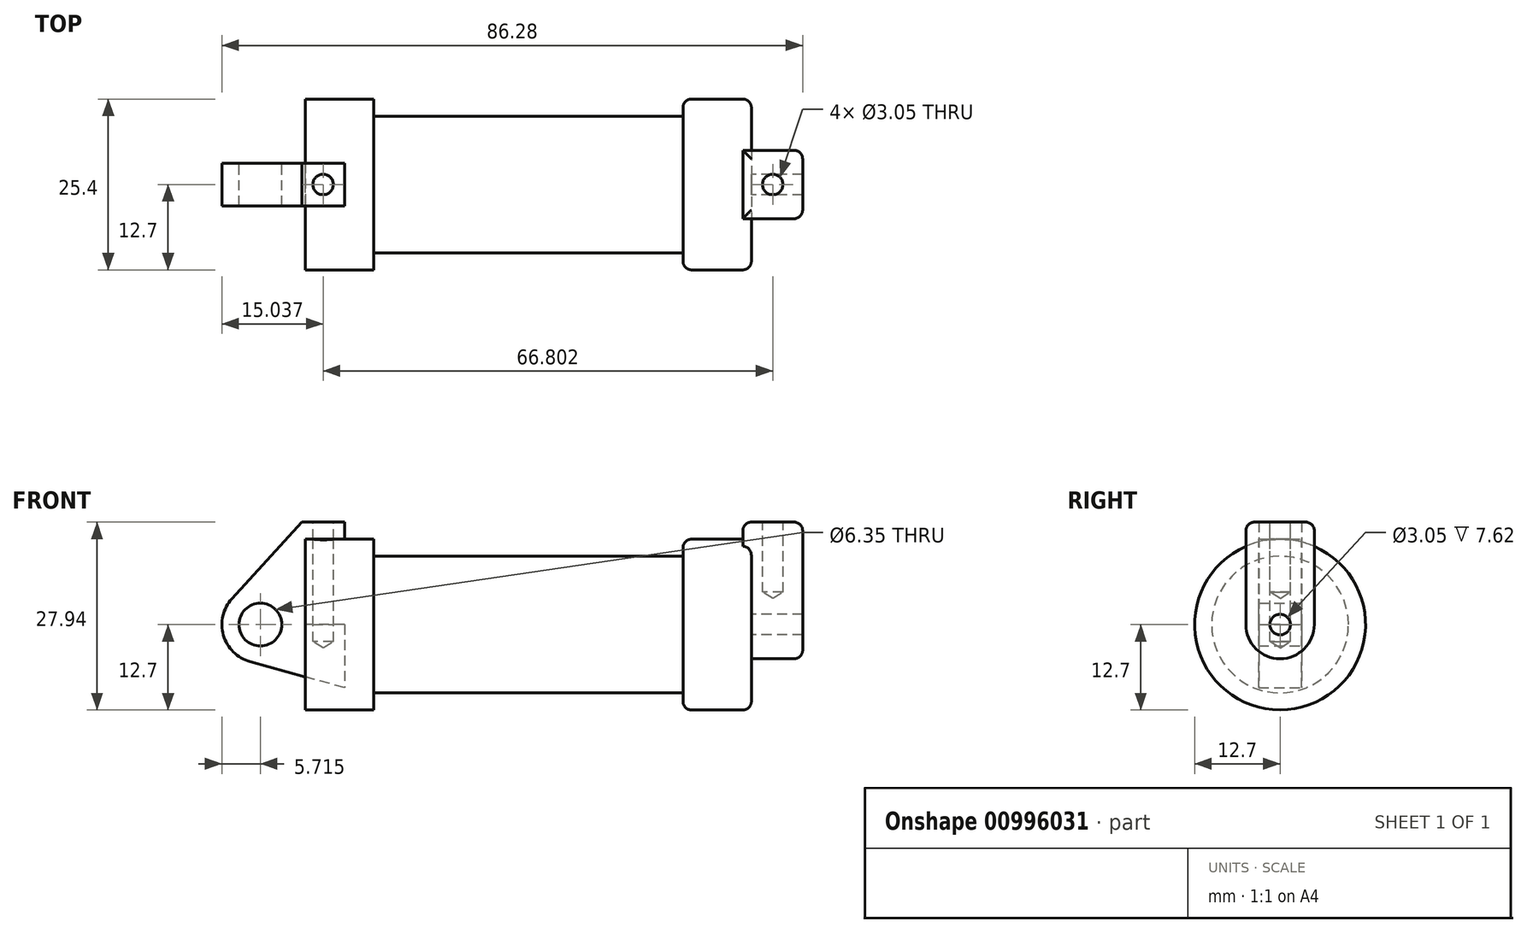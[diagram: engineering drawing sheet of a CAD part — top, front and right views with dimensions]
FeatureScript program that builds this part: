
annotation { "Feature Type Name" : "Feature", "Feature Type Description" : "" }
export const myFeature = defineFeature(function(context is Context, id is Id, definition is map)
    precondition{}
    {
        {
            var Q0;
            Q0=qCreatedBy(makeId("Front.planeOp"),FACE);
            var sketch = newSketch(context, id + "F0", { "sketchPlane" : qUnion([Q0])});
            skLineSegment(sketch, "E0", {"start": v(0, 0) * mm, "end": v(0, 12.7) * mm});
            skLineSegment(sketch, "E1", {"start": v(0, 12.7) * mm, "end": v(10.16, 12.7) * mm});
            skLineSegment(sketch, "E2", {"start": v(10.16, 12.7) * mm, "end": v(10.16, 10.16) * mm});
            skLineSegment(sketch, "E3", {"start": v(10.16, 10.16) * mm, "end": v(56.13, 10.16) * mm});
            skLineSegment(sketch, "E4", {"start": v(56.13, 10.16) * mm, "end": v(56.13, 12.7) * mm});
            skLineSegment(sketch, "E5", {"start": v(56.13, 12.7) * mm, "end": v(66.3, 12.7) * mm});
            skLineSegment(sketch, "E6", {"start": v(66.3, 12.7) * mm, "end": v(66.3, 0) * mm});
            skLineSegment(sketch, "E7", {"start": v(66.3, 0) * mm, "end": v(0, 0) * mm});
            skLineSegment(sketch, "E8", {"start": v(5.84, 15.24) * mm, "end": v(-0.5, 15.24) * mm});
            skLineSegment(sketch, "E9", {"start": v(-0.5, 15.24) * mm, "end": v(-10.88, 3.85) * mm});
            skLineSegment(sketch, "E10", {"start": v(0, 0) * mm, "end": v(-6.65, 0) * mm});
            skCircle(sketch, "E11", {"center": v(-6.65, 0) * mm, "radius": 5.72 * mm});
            skCircle(sketch, "E12", {"center": v(-6.65, 0) * mm, "radius": 3.18 * mm});
            skLineSegment(sketch, "E13", {"start": v(5.84, 15.24) * mm, "end": v(5.84, -9.4) * mm});
            skLineSegment(sketch, "E14", {"start": v(5.84, -9.4) * mm, "end": v(-8.18, -5.5) * mm});
            skSolve(sketch);
        }
        {
            var Q0;
            {var subQ0=sQuery(id+"F0.wireOp",EDGE,"E0");Q0=makeQuery(id+"F0.imprint","IMPRINT",FACE,{"disambiguationData":[TD([[makeQuery(id+"F0.imprint","IMPRINT",EDGE,{"derivedFrom":subQ0}),-1.0]])]});}
            var Q1;
            {var subQ0=sQuery(id+"F0.wireOp",EDGE,"E2");Q1=makeQuery(id+"F0.imprint","IMPRINT",FACE,{"disambiguationData":[TD([[makeQuery(id+"F0.imprint","IMPRINT",EDGE,{"derivedFrom":subQ0}),-1.0]])]});}
            var Q2;
            Q2=sQuery(id+"F0.wireOp",EDGE,"E7");
            revolve(context, id + "F1", {"surfaceOperationType" : NewSurfaceOperationType.NEW, "entities" : qUnion([Q0, Q1]), "axis" : qUnion([Q2]), "revolveType" : RevolveType.FULL});
        }
        {
            var Q0;
            {var subQ1=sQuery(id+"F0.wireOp",EDGE,"E0");Q0=makeQuery(id+"F0.imprint","IMPRINT",FACE,{"disambiguationData":[TD([[makeQuery(id+"F0.imprint","IMPRINT",EDGE,{"derivedFrom":subQ1}),1.0]])]});}
            var Q1;
            {var subQ5=sQuery(id+"F0.wireOp",EDGE,"E12");Q1=makeQuery(id+"F0.imprint","IMPRINT",FACE,{"disambiguationData":[TD([[makeQuery(id+"F0.imprint","IMPRINT",EDGE,{"derivedFrom":subQ5}),-1.0]])]});}
            var Q2;
            {var subQ0=sQuery(id+"F0.wireOp",EDGE,"E14");Q2=makeQuery(id+"F0.imprint","IMPRINT",FACE,{"disambiguationData":[TD([[makeQuery(id+"F0.imprint","IMPRINT",EDGE,{"derivedFrom":subQ0}),-1.0]])]});}
            extrude(context, id + "F2", {"entities" : qUnion([Q0, Q1, Q2]), "endBound" : BoundingType.SYMMETRIC, "depth" : 6.35 * mm, "offsetDistance" : 25.4 * mm});
        }
        {
            var Q0;
            Q0=makeQuery(id+"F1.opRevolve","SWEPT_FACE",FACE,{"disambiguationData":[OSD([sQuery(id+"F0.wireOp",EDGE,"E6")])]});
            var sketch = newSketch(context, id + "F3", { "sketchPlane" : qUnion([Q0])});
            skCircle(sketch, "E15", {"center": v(0, 0) * mm, "radius": 1.52 * mm});
            skCircle(sketch, "E16", {"center": v(0, 0) * mm, "radius": 5.08 * mm});
            skLineSegment(sketch, "E17", {"start": v(5.08, 0) * mm, "end": v(5.08, 15.24) * mm});
            skLineSegment(sketch, "E18", {"start": v(5.08, 15.24) * mm, "end": v(-5.08, 15.24) * mm});
            skLineSegment(sketch, "E19", {"start": v(-5.08, 15.24) * mm, "end": v(-5.08, 0) * mm});
            skSolve(sketch);
        }
        {
            var Q0;
            {var subQ0=sQuery(id+"F3.wireOp",EDGE,"E17");var subQ1=sQuery(id+"F3.wireOp",EDGE,"E16");var subQ2=makeQuery(id+"F3.imprint","INTERSECT",VERTEX,{"derivedFrom":[subQ1,subQ0]});Q0=makeQuery(id+"F3.imprint","IMPRINT",FACE,{"disambiguationData":[TD([[makeQuery(id+"F3.imprint","IMPRINT",EDGE,{"disambiguationData":[TD([[subQ2,-1.0]])],"derivedFrom":subQ1}),-1.0]])]});}
            var Q1;
            {var subQ0=sQuery(id+"F3.wireOp",EDGE,"E18");Q1=makeQuery(id+"F3.imprint","IMPRINT",FACE,{"disambiguationData":[TD([[makeQuery(id+"F3.imprint","IMPRINT",EDGE,{"derivedFrom":subQ0}),1.0]])]});}
            var Q2;
            Q2=makeQuery(id+"F3.imprint","IMPRINT",FACE,{"disambiguationData":[TD([[makeQuery(id+"F3.imprint","IMPRINT",EDGE,{"derivedFrom":sQuery(id+"F3.wireOp",EDGE,"E15")}),-1.0]])]});
            extrude(context, id + "F4", {"entities" : qUnion([Q0, Q1, Q2]), "operationType" : NewBodyOperationType.ADD, "depth" : 7.62 * mm, "offsetDistance" : 25.4 * mm});
        }
        {
            var Q0;
            Q0=makeQuery(id+"F4.opExtrude","CAP_FACE",FACE,{"disambiguationData":[OSD([sQuery(id+"F3.wireOp",EDGE,"E15"),sQuery(id+"F3.wireOp",EDGE,"E16"),sQuery(id+"F3.wireOp",EDGE,"E17"),sQuery(id+"F3.wireOp",EDGE,"E18"),sQuery(id+"F3.wireOp",EDGE,"E19")])],"isStart":true});
            extrude(context, id + "F5", {"entities" : qUnion([Q0]), "operationType" : NewBodyOperationType.ADD, "depth" : 1.27 * mm, "offsetDistance" : 25.4 * mm});
        }
        {
            var Q0;
            Q0=makeQuery(id+"F2.opExtrude","SWEPT_FACE",FACE,{"disambiguationData":[OSD([sQuery(id+"F0.wireOp",EDGE,"E8")])]});
            var sketch = newSketch(context, id + "F6", { "sketchPlane" : qUnion([Q0])});
            skPoint(sketch, "E20", {"position": v(2.67, 0) * mm});
            skPoint(sketch, "E20.positionSnap0", {"position": v(-0.5, 0) * mm});
            skPoint(sketch, "E20.positionSnap1", {"position": v(2.67, 3.18) * mm});
            skSolve(sketch);
        }
        {
            var Q0;
            Q0=sQuery(id+"F6.wireOp",VERTEX,"E20");
            var Q1;
            Q1=makeQuery(id+"F1.opRevolve","SWEPT_BODY",BODY,{"disambiguationData":[OSD([sQuery(id+"F0.wireOp",EDGE,"E0"),sQuery(id+"F0.wireOp",EDGE,"E1"),sQuery(id+"F0.wireOp",EDGE,"E2"),sQuery(id+"F0.wireOp",EDGE,"E3"),sQuery(id+"F0.wireOp",EDGE,"E4"),sQuery(id+"F0.wireOp",EDGE,"E5"),sQuery(id+"F0.wireOp",EDGE,"E6"),sQuery(id+"F0.wireOp",EDGE,"E7")])]});
            var Q2;
            Q2=makeQuery(id+"F2.opExtrude","SWEPT_BODY",BODY,{"disambiguationData":[OSD([sQuery(id+"F0.wireOp",EDGE,"E0"),sQuery(id+"F0.wireOp",EDGE,"E1"),sQuery(id+"F0.wireOp",EDGE,"E7"),sQuery(id+"F0.wireOp",EDGE,"E8"),sQuery(id+"F0.wireOp",EDGE,"E9"),sQuery(id+"F0.wireOp",EDGE,"E11"),sQuery(id+"F0.wireOp",EDGE,"E12"),sQuery(id+"F0.wireOp",EDGE,"E13"),sQuery(id+"F0.wireOp",EDGE,"E14")])]});
            hole(context, id + "F7", {"style" : HoleStyle.SIMPLE, "endStyle" : HoleEndStyle.BLIND, "holeDiameter" : 3.05 * mm, "majorDiameter" : 6.35 * mm, "holeDepth" : 17.78 * mm, "isTappedThrough" : true, "tappedDepth" : 12.7 * mm, "tapClearance" : 3, "startFromSketch" : true, "locations" : qUnion([Q0]), "scope" : qUnion([Q1, Q2])});
        }
        {
            var Q0;
            {var subQ0=sQuery(id+"F3.wireOp",EDGE,"E18");Q0=makeQuery(id+"F5.boolean.opBoolean","MERGE",FACE,{"derivedFrom":[makeQuery(id+"F4.opExtrude","SWEPT_FACE",FACE,{"disambiguationData":[OSD([subQ0])]}),makeQuery(id+"F5.opExtrude","SWEPT_FACE",FACE,{"disambiguationData":[OSD([subQ0])]})]});}
            var sketch = newSketch(context, id + "F8", { "sketchPlane" : qUnion([Q0])});
            skPoint(sketch, "E21", {"position": v(69.47, 0) * mm});
            skPoint(sketch, "E21.positionSnap0", {"position": v(69.47, 5.08) * mm});
            skPoint(sketch, "E21.positionSnap1", {"position": v(65.02, 0) * mm});
            skSolve(sketch);
        }
        {
            var Q0;
            Q0=sQuery(id+"F8.wireOp",VERTEX,"E21");
            var Q1;
            Q1=makeQuery(id+"F1.opRevolve","SWEPT_BODY",BODY,{"disambiguationData":[OSD([sQuery(id+"F0.wireOp",EDGE,"E0"),sQuery(id+"F0.wireOp",EDGE,"E1"),sQuery(id+"F0.wireOp",EDGE,"E2"),sQuery(id+"F0.wireOp",EDGE,"E3"),sQuery(id+"F0.wireOp",EDGE,"E4"),sQuery(id+"F0.wireOp",EDGE,"E5"),sQuery(id+"F0.wireOp",EDGE,"E6"),sQuery(id+"F0.wireOp",EDGE,"E7")])]});
            hole(context, id + "F9", {"style" : HoleStyle.SIMPLE, "endStyle" : HoleEndStyle.BLIND, "holeDiameter" : 3.05 * mm, "majorDiameter" : 6.35 * mm, "holeDepth" : 10.4 * mm, "isTappedThrough" : true, "tappedDepth" : 12.7 * mm, "tapClearance" : 3, "startFromSketch" : true, "locations" : qUnion([Q0]), "scope" : qUnion([Q1])});
        }
        {
            var Q0;
            {var subQ0=sQuery(id+"F0.wireOp",EDGE,"E5");var subQ1=sQuery(id+"F0.wireOp",EDGE,"E6");Q0=makeQuery(id+"F4.boolean.opBoolean","SPLIT",EDGE,{"disambiguationData":[topologyDisambiguationEdgeConnected([makeQuery(id+"F1.opRevolve","SWEPT_FACE",FACE,{"disambiguationData":[OSD([subQ1])]})])],"derivedFrom":makeQuery(id+"F1.opRevolve","SWEPT_EDGE",EDGE,{"disambiguationData":[OSD([subQ0,subQ1])]})});}
            var Q1;
            Q1=makeQuery(id+"F1.opRevolve","SWEPT_EDGE",EDGE,{"disambiguationData":[OSD([sQuery(id+"F0.wireOp",EDGE,"E4"),sQuery(id+"F0.wireOp",EDGE,"E5")])]});
            var Q2;
            Q2=makeQuery(id+"F4.opExtrude","CAP_EDGE",EDGE,{"disambiguationData":[OSD([sQuery(id+"F3.wireOp",EDGE,"E18")])],"isStart":false});
            var Q3;
            Q3=makeQuery(id+"F5.opExtrude","CAP_EDGE",EDGE,{"disambiguationData":[OSD([sQuery(id+"F3.wireOp",EDGE,"E18")])],"isStart":false});
            var Q4;
            {var subQ0=sQuery(id+"F3.wireOp",EDGE,"E19");var subQ1=sQuery(id+"F3.wireOp",EDGE,"E18");Q4=makeQuery(id+"F5.boolean.opBoolean","MERGE",EDGE,{"derivedFrom":[makeQuery(id+"F4.opExtrude","SWEPT_EDGE",EDGE,{"disambiguationData":[OSD([subQ1,subQ0])]}),makeQuery(id+"F5.opExtrude","SWEPT_EDGE",EDGE,{"disambiguationData":[OSD([subQ1,subQ0])]})]});}
            var Q5;
            {var subQ0=sQuery(id+"F3.wireOp",EDGE,"E18");var subQ1=sQuery(id+"F3.wireOp",EDGE,"E17");Q5=makeQuery(id+"F5.boolean.opBoolean","MERGE",EDGE,{"derivedFrom":[makeQuery(id+"F4.opExtrude","SWEPT_EDGE",EDGE,{"disambiguationData":[OSD([subQ1,subQ0])]}),makeQuery(id+"F5.opExtrude","SWEPT_EDGE",EDGE,{"disambiguationData":[OSD([subQ1,subQ0])]})]});}
            var Q6;
            Q6=makeQuery(id+"F4.opExtrude","CAP_EDGE",EDGE,{"disambiguationData":[OSD([sQuery(id+"F3.wireOp",EDGE,"E19")])],"isStart":false});
            fillet(context, id + "F10", {"entities" : qUnion([Q0, Q1, Q2, Q3, Q4, Q5, Q6]), "radius" : 1.27 * mm, "tangentPropagation" : true, "allowEdgeOverflow" : false});
        }
    });
